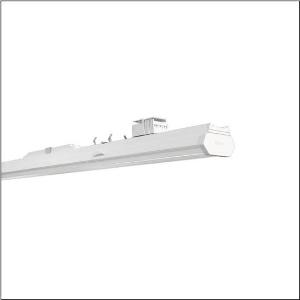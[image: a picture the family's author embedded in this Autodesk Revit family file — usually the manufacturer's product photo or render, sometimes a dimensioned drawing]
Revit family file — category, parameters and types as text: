
# Revit family: licross_21_protected_mo_52tp11dn4a5g
name_source: partatom
category: Lighting Fixtures
units: mm (PartAtom-declared; Revit-internal decimal feet)

## family parameters
Cut with Voids When Loaded = No
Host = Face
Light Source = No
Part Type = Normal
Room Calculation Point = No
Round Connector Dimension = Use Diameter
Shared = No

## types (1)
- --- (1 x LED, 10650 lm, 62 W, 4000K)
    Apparent Load = 62 VA
    CIE Flux Codes = 83 94 98 100 100
    Color Rendering = 80
    Color Temperature = 4000K
    Default Elevation = 1800 mm
    Description = Licross 21 Protected MO, luminaire insert, of sheet steel, galvanised, coil coated, white, length: 1.500mm, width: 90mm, height: 103mm, LED rated luminous flux: 10.650lm, light colour: 840, SDCM (Standard Deviation of Colour Matching)MacAdam ≤ 3 SDCM (initial), control gear: DALI 2, with plug, 5-pole, with phase selection, mains connection: 220..240V, AC, 50/60Hz, rated input power: 62W, internal wiring halogen-free, primary light control with lens, of plastic, primary optical cover: cover, of PMMA, light emission: direct distribution, primary light characteristic: symmetric, protection rating (complete): IP64, insulation class (complete): insulation class I (protective earthing), certification: CE, ENEC, VDE, UKCA, protection symbol: D if used in an environment with conductive dust loads with corresponding accessories, impact resistance: IK06, permissible ambient temperature for indoor applications: -25..+35°C, corresponds to IFS (International Featured Standards) requirements for safety and quality in the food industry, reducing of maximum allowable ambient temperature of 5°C with ceiling mounting, LABS conformity tested according to VDMA 24364:2018-05, The light source and the operating device comply with the requirements of the Ecodesign Regulation (EU) 2019/2020 and are replaceable in accordance with this regulation, packaging unit: 1 piece
    Height = 92 mm
    Lamp = 1 x LED
    Lamp Light Flux = 10650 lm
    Lamp Power = 62 W
    Lamp count = 1
    Length = 1500 mm
    Luminous efficacy = 172 lm/W
    Manufacturer = Siteco
    ModVariant = No
    Model = 52TP11DN4A5G
    Mounting Place = Ceiling
    Mounting Type = Pendant
    Number of Poles = 1
    OnlyDefault = Yes
    Power Factor = 1
    Product Name = Licross 21 Protected MO
    Product group = luminaire insert | ceiling pendant
    ProductGroupID = 901
    Protection Class = Protection class I
    Protection Degree = IP 64
    RLX_Detail_Level = 1
    RLX_Emergency_Light_Flux = 0 lm
    RLX_Emergency_Type = 0
    RLX_Emergency_Type_DB = No
    RlxData = <blob elided: 24361 chars, md5=16e59d02>
    Socket = socket
    Standby Power = 0 W
    System Light Flux = 10650 lm
    System Power = 62 W
    Type Comments = factory setting: luminous flux: 100 % | dim-lin: 254 | 418 mA
    Type Image = l_1256148.jpg
    URL = http://relux.com
    VarID = @adj_129939
    Voltage = 0 V
    Weight = 0.00 kg
    Width = 88 mm

## geometry (parser evidence)
native form markers: Blend x4, Sweep x11
no freeform markers — native parametric forms only
